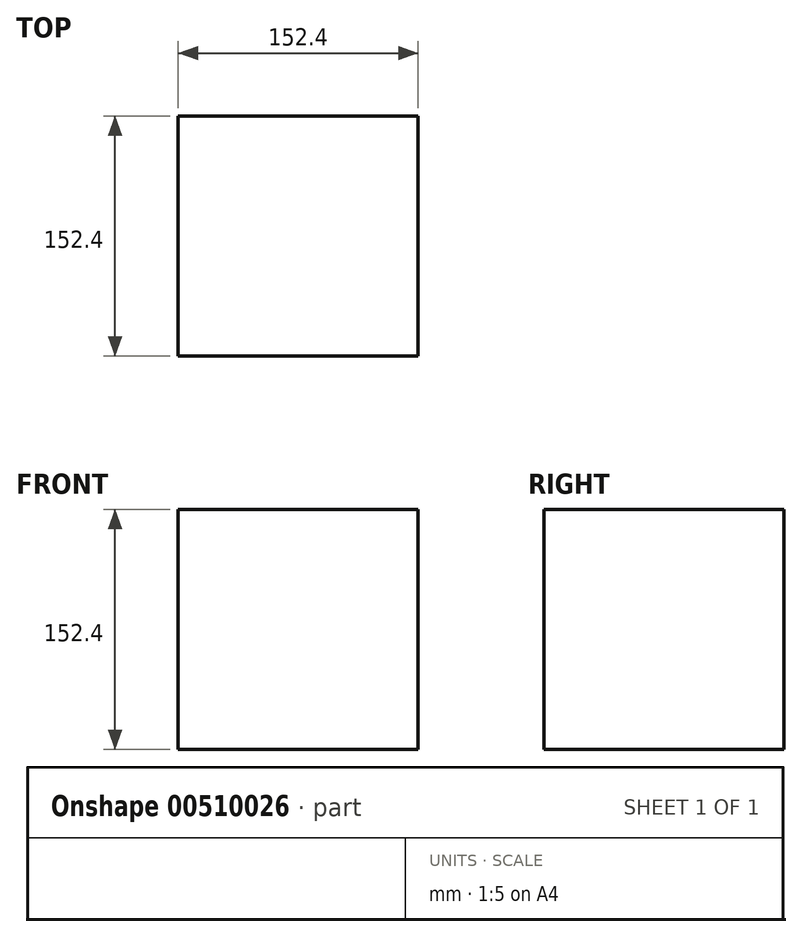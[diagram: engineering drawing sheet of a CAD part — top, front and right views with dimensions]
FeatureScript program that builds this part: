
annotation { "Feature Type Name" : "Feature", "Feature Type Description" : "" }
export const myFeature = defineFeature(function(context is Context, id is Id, definition is map)
    precondition{}
    {
        {
            var Q0;
            Q0=qCreatedBy(makeId("Top.planeOp"),FACE);
            var sketch = newSketch(context, id + "F0", { "sketchPlane" : qUnion([Q0])});
            skLineSegment(sketch, "E0.bottom", {"start": v(76.2, 76.2) * mm, "end": v(-76.2, 76.2) * mm});
            skLineSegment(sketch, "E0.top", {"start": v(76.2, -76.2) * mm, "end": v(-76.2, -76.2) * mm});
            skLineSegment(sketch, "E0.left", {"start": v(76.2, 76.2) * mm, "end": v(76.2, -76.2) * mm});
            skLineSegment(sketch, "E0.right", {"start": v(-76.2, 76.2) * mm, "end": v(-76.2, -76.2) * mm});
            skPoint(sketch, "E0.middle", {"position": v(0, 0) * mm});
            skSolve(sketch);
        }
        {
            var Q0;
            Q0=makeQuery(id+"F0.imprint","IMPRINT",FACE,{"disambiguationData":[TD([[makeQuery(id+"F0.imprint","IMPRINT",EDGE,{"derivedFrom":sQuery(id+"F0.wireOp",EDGE,"E0.bottom")}),1.0]])]});
            extrude(context, id + "F1", {"entities" : qUnion([Q0]), "depth" : 152.4 * mm});
        }
    });
